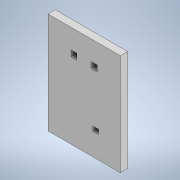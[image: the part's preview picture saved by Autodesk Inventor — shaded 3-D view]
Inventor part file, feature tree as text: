
AUTODESK INVENTOR PART (.ipt)
format: ipt  version: 2020 (Build 240168000, 168)  size: 170,496 bytes
history: native  units: in
note: dims shown in document units (in); Inventor stores cm internally (conversion verified against a paired STEP export)
features: extrude x6, sketch x6
ambient origin geometry x8: Origin, YZ Plane, XZ Plane, XY Plane, X Axis, Y Axis, Z Axis, Center Point
bodies: Solid1 (feature_tree)
feature tree (12):
  extrude  "Extrusion1"  Depth=1.2205in
  extrude  "Extrusion2"  Depth=0.4724in
  extrude  "Extrusion3"  Depth=0.1969in
  extrude  "Extrusion4"  Depth=0.0984in
  extrude  "Extrusion5"  Depth=0.0591in TaperAngle=0.0deg
  extrude  "Extrusion6"  Depth=0.1575in
  sketch  "Sketch1"  dims[d0=0.6693in d1=1.2205in]
  sketch  "Sketch2"  dims[d2=0.0591in d3=0.0in d4=0.4724in]
  sketch  "Sketch3"  dims[d5=0.315in d6=0.1969in]
  sketch  "Sketch4"  dims[d7=0.6693in d8=0.0984in]
  sketch  "Sketch5"  dims[d9=0.1772in d10=0.0591in d11=0.0in]
  sketch  "Sketch6"  dims[d12=0.1575in d13=0.1575in d14=0.1575in d15=0.0984in d16=0.0in d17=0.0394in d18=0.0in d19=0.0787in d20=0.0591in d21=0.1083in d23=0.0in d24=0.0in d25=0.0394in d26=0.1083in d27=0.0787in d28=0.0787in d30=0.1575in d31=0.0in d32=0.0in]
